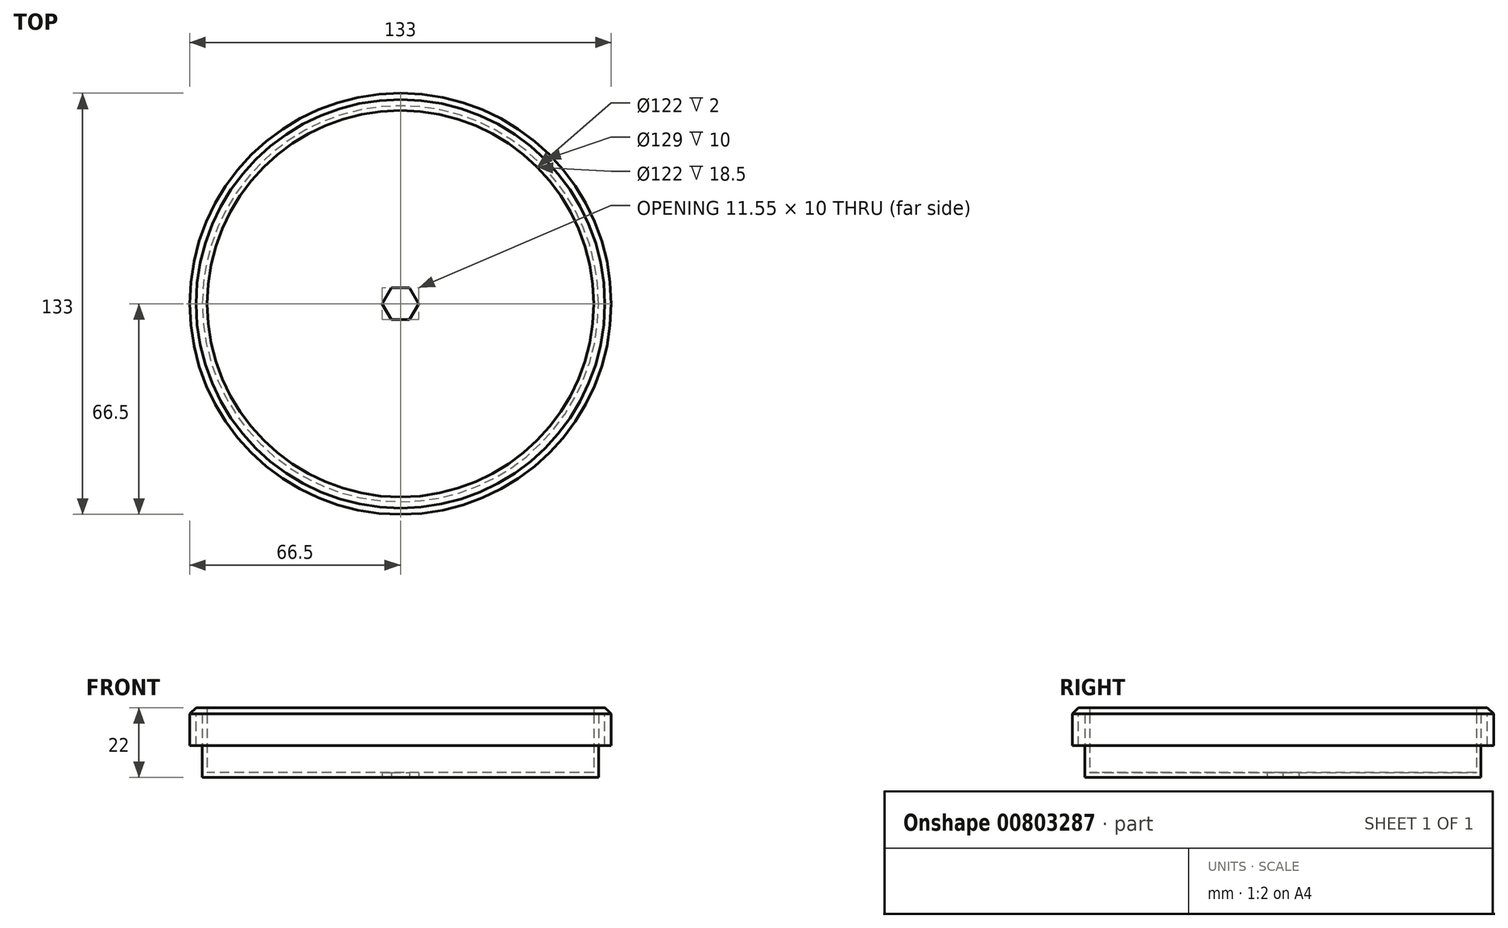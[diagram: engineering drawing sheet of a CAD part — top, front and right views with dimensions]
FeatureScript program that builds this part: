
annotation { "Feature Type Name" : "Feature", "Feature Type Description" : "" }
export const myFeature = defineFeature(function(context is Context, id is Id, definition is map)
    precondition{}
    {
        {
            var Q0;
            Q0=qCreatedBy(makeId("Top.planeOp"),FACE);
            var sketch = newSketch(context, id + "F0", { "sketchPlane" : qUnion([Q0])});
            skCircle(sketch, "E0", {"center": v(0, 0) * mm, "radius": 62.5 * mm});
            skCircle(sketch, "E1.cCircle", {"center": v(0, 0) * mm, "radius": 5 * mm, "construction": true});
            skLineSegment(sketch, "E1.0", {"start": v(2.89, -5) * mm, "end": v(-2.89, -5) * mm});
            skLineSegment(sketch, "E1.1", {"start": v(-2.89, -5) * mm, "end": v(-5.77, 0) * mm});
            skLineSegment(sketch, "E1.2", {"start": v(-5.77, 0) * mm, "end": v(-2.89, 5) * mm});
            skLineSegment(sketch, "E1.3", {"start": v(-2.89, 5) * mm, "end": v(2.89, 5) * mm});
            skLineSegment(sketch, "E1.4", {"start": v(2.89, 5) * mm, "end": v(5.77, 0) * mm});
            skLineSegment(sketch, "E1.5", {"start": v(5.77, 0) * mm, "end": v(2.89, -5) * mm});
            skPoint(sketch, "E1.0.midPoint", {"position": v(0, -5) * mm});
            skSolve(sketch);
        }
        {
            var Q0;
            Q0=makeQuery(id+"F0.imprint","IMPRINT",FACE,{"disambiguationData":[TD([[makeQuery(id+"F0.imprint","IMPRINT",EDGE,{"derivedFrom":sQuery(id+"F0.wireOp",EDGE,"E0")}),1.0]])]});
            var Q1;
            Q1=makeQuery(id+"F0.imprint","IMPRINT",FACE,{"disambiguationData":[TD([[makeQuery(id+"F0.imprint","IMPRINT",EDGE,{"derivedFrom":sQuery(id+"F0.wireOp",EDGE,"E1.0")}),-1.0]])]});
            extrude(context, id + "F1", {"entities" : qUnion([Q0, Q1]), "depth" : 20 * mm, "offsetDistance" : 25 * mm});
        }
        {
            var Q0;
            Q0=makeQuery(id+"F1.opExtrude","CAP_FACE",FACE,{"disambiguationData":[OSD([sQuery(id+"F0.wireOp",EDGE,"E0")])],"isStart":false});
            shell(context, id + "F2", {"entities" : qUnion([Q0]), "thickness" : 1.5 * mm});
        }
        {
            var Q0;
            Q0=makeQuery(id+"F0.imprint","IMPRINT",FACE,{"disambiguationData":[TD([[makeQuery(id+"F0.imprint","IMPRINT",EDGE,{"derivedFrom":sQuery(id+"F0.wireOp",EDGE,"E1.0")}),-1.0]])]});
            extrude(context, id + "F3", {"entities" : qUnion([Q0]), "operationType" : NewBodyOperationType.REMOVE, "depth" : 25 * mm, "offsetDistance" : 25 * mm});
        }
        {
            var Q0;
            Q0=makeQuery(id+"F1.opExtrude","CAP_FACE",FACE,{"disambiguationData":[OSD([sQuery(id+"F0.wireOp",EDGE,"E0")])],"isStart":false});
            var sketch = newSketch(context, id + "F4", { "sketchPlane" : qUnion([Q0])});
            skCircle(sketch, "E2.0", {"center": v(0, 0) * mm, "radius": 62.5 * mm, "construction": true});
            skCircle(sketch, "E3.0", {"center": v(0, 0) * mm, "radius": 64.5 * mm});
            skCircle(sketch, "E4.0", {"center": v(0, 0) * mm, "radius": 66.5 * mm});
            skCircle(sketch, "E5.0", {"center": v(0, 0) * mm, "radius": 61 * mm});
            skSolve(sketch);
        }
        {
            var Q0;
            Q0 = qSketchRegion(id + "F4", true);
            var Q1;
            Q1=makeQuery(id+"F4.imprint","IMPRINT",FACE,{"disambiguationData":[TD([[makeQuery(id+"F4.imprint","IMPRINT",EDGE,{"derivedFrom":sQuery(id+"F4.wireOp",EDGE,"E3.0")}),1.0]])]});
            var Q2;
            Q2=makeQuery(id+"F4.imprint","IMPRINT",FACE,{"disambiguationData":[TD([[makeQuery(id+"F4.imprint","IMPRINT",EDGE,{"derivedFrom":sQuery(id+"F4.wireOp",EDGE,"E5.0")}),-1.0]])]});
            extrude(context, id + "F5", {"entities" : qUnion([Q0, Q1, Q2]), "depth" : 2 * mm, "offsetDistance" : 25 * mm});
        }
        {
            var Q0;
            Q0=makeQuery(id+"F4.imprint","IMPRINT",FACE,{"disambiguationData":[TD([[makeQuery(id+"F4.imprint","IMPRINT",EDGE,{"derivedFrom":sQuery(id+"F4.wireOp",EDGE,"E3.0")}),-1.0]])]});
            extrude(context, id + "F6", {"entities" : qUnion([Q0]), "operationType" : NewBodyOperationType.ADD, "oppositeDirection" : true, "depth" : 10 * mm, "offsetDistance" : 25 * mm});
        }
        {
            var Q0;
            Q0=makeQuery(id+"F5.opExtrude","CAP_EDGE",EDGE,{"disambiguationData":[OSD([sQuery(id+"F4.wireOp",EDGE,"E4.0")])],"isStart":false});
            chamfer(context, id + "F7", {"entities" : qUnion([Q0]), "width" : 2 * mm, "tangentPropagation" : true});
        }
    });
